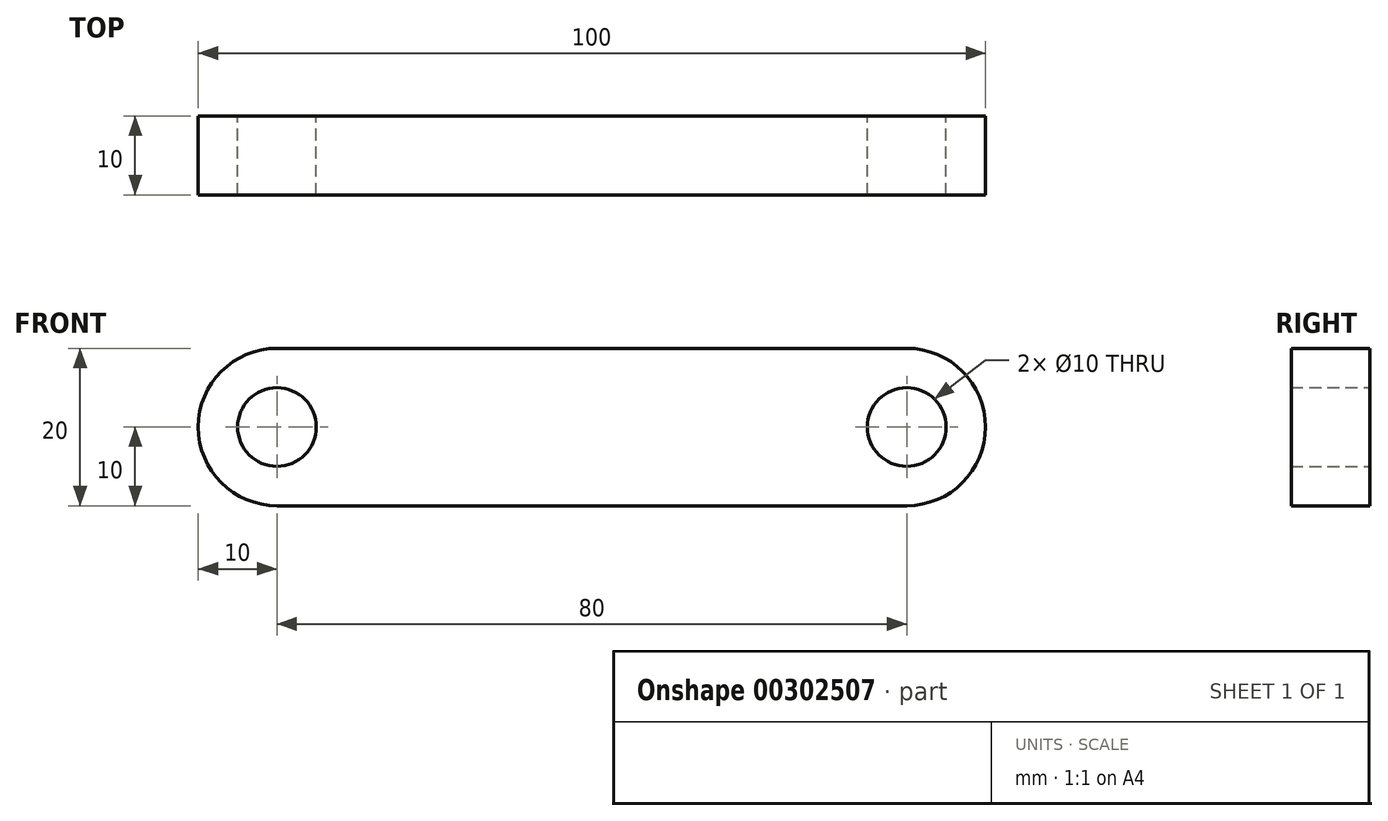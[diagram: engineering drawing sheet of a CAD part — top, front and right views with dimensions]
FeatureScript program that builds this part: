
annotation { "Feature Type Name" : "Feature", "Feature Type Description" : "" }
export const myFeature = defineFeature(function(context is Context, id is Id, definition is map)
    precondition{}
    {
        {
            var Q0;
            Q0=qCreatedBy(makeId("Front.planeOp"),FACE);
            var sketch = newSketch(context, id + "F0", { "sketchPlane" : qUnion([Q0])});
            skLineSegment(sketch, "E0.bottom", {"start": v(0, 0) * mm, "end": v(80, 0) * mm});
            skLineSegment(sketch, "E0.top", {"start": v(0, 20) * mm, "end": v(80, 20) * mm});
            skArc(sketch, "E1", {"start": v(0, 20) * mm, "mid": v(-10, 10) * mm, "end": v(0, 0) * mm});
            skArc(sketch, "E2", {"start": v(80, 0) * mm, "mid": v(90, 10) * mm, "end": v(80, 20) * mm});
            skCircle(sketch, "E3", {"center": v(0, 10) * mm, "radius": 5 * mm});
            skCircle(sketch, "E4", {"center": v(80, 10) * mm, "radius": 5 * mm});
            skSolve(sketch);
        }
        {
            var Q0;
            Q0 = qSketchRegion(id + "F0", true);
            extrude(context, id + "F1", {"entities" : qUnion([Q0]), "depth" : 10 * mm});
        }
    });
